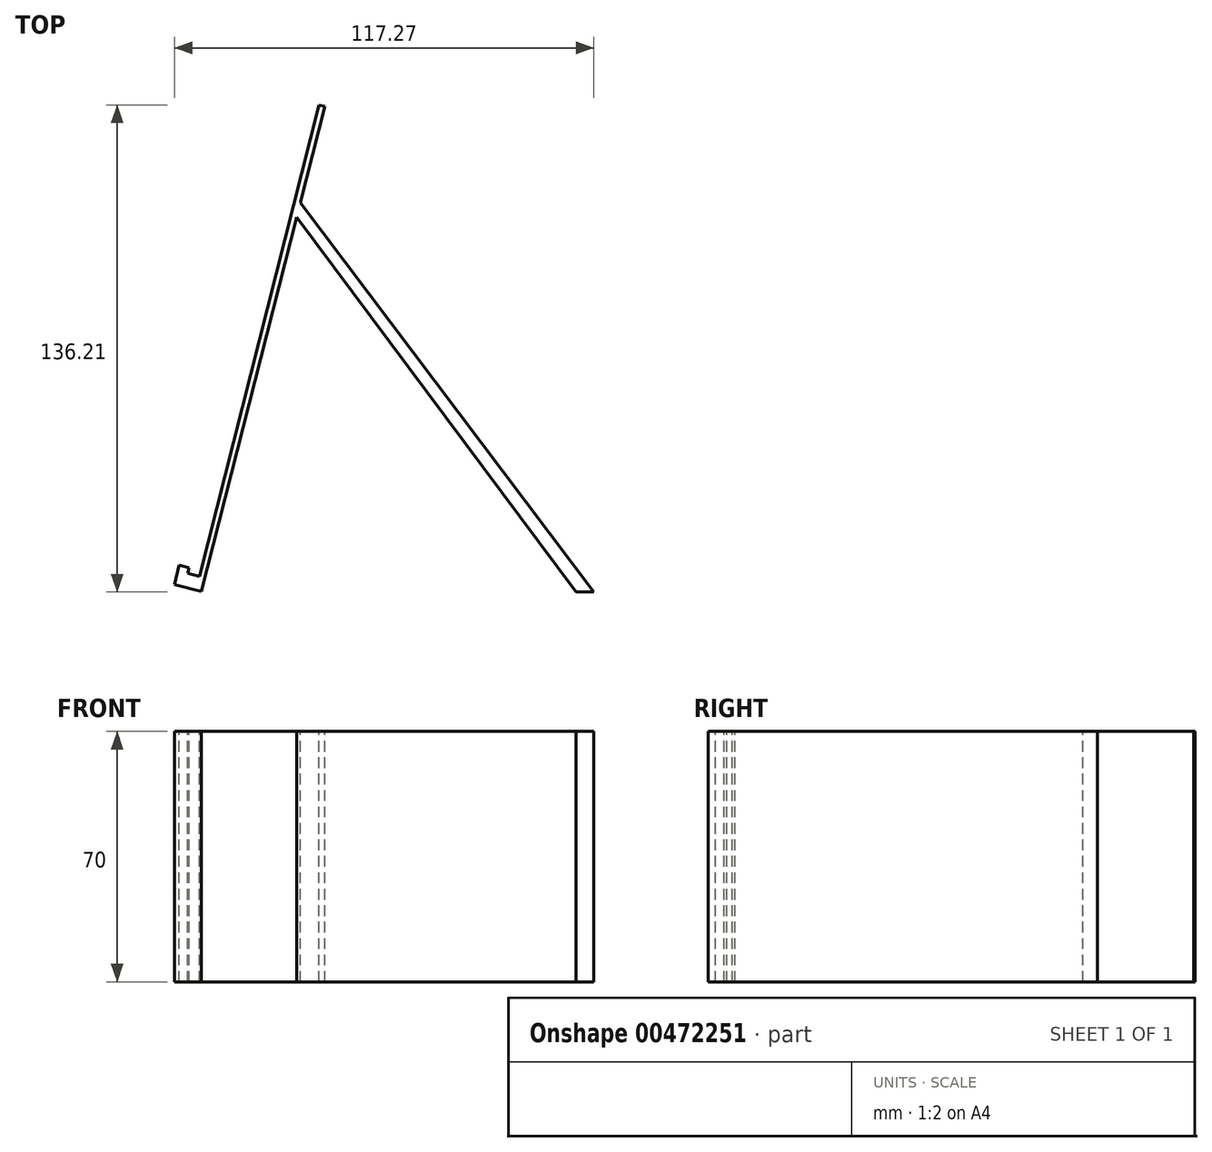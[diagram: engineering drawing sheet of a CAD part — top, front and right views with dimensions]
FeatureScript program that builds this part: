
annotation { "Feature Type Name" : "Feature", "Feature Type Description" : "" }
export const myFeature = defineFeature(function(context is Context, id is Id, definition is map)
    precondition{}
    {
        {
            var Q0;
            Q0=qCreatedBy(makeId("Top.planeOp"),FACE);
            var sketch = newSketch(context, id + "F0", { "sketchPlane" : qUnion([Q0])});
            skLineSegment(sketch, "E0", {"start": v(-45.52, -67.71) * mm, "end": v(-18.92, 37) * mm});
            skLineSegment(sketch, "E1", {"start": v(-18.92, 37) * mm, "end": v(59.18, -67.84) * mm});
            skLineSegment(sketch, "E2", {"start": v(-45.52, -67.71) * mm, "end": v(-53.1, -65.79) * mm});
            skLineSegment(sketch, "E3", {"start": v(-53.1, -65.79) * mm, "end": v(-52.1, -61.9) * mm});
            skLineSegment(sketch, "E4", {"start": v(-49.3, -62.6) * mm, "end": v(-46.09, -63.42) * mm});
            skLineSegment(sketch, "E5", {"start": v(-11.05, 67.98) * mm, "end": v(-12.6, 68.37) * mm});
            skLineSegment(sketch, "E6", {"start": v(-12.6, 68.37) * mm, "end": v(-46.09, -63.42) * mm});
            skPoint(sketch, "E7.endSnap0", {"position": v(-49.3, -66.75) * mm});
            skLineSegment(sketch, "E8", {"start": v(-49.3, -62.6) * mm, "end": v(-48.91, -61.05) * mm});
            skLineSegment(sketch, "E9", {"start": v(-52.1, -61.9) * mm, "end": v(-51.7, -60.35) * mm});
            skLineSegment(sketch, "E10", {"start": v(-48.91, -61.05) * mm, "end": v(-51.7, -60.35) * mm});
            skLineSegment(sketch, "E11", {"start": v(59.18, -67.84) * mm, "end": v(64.18, -67.84) * mm});
            skLineSegment(sketch, "E12", {"start": v(64.18, -67.84) * mm, "end": v(-17.9, 41.02) * mm});
            skLineSegment(sketch, "E13.trimOffspring", {"start": v(-17.9, 41.02) * mm, "end": v(-11.05, 67.98) * mm});
            skSolve(sketch);
        }
        {
            var Q0;
            Q0=makeQuery(id+"F0.imprint","IMPRINT",FACE,{"disambiguationData":[TD([[makeQuery(id+"F0.imprint","IMPRINT",EDGE,{"derivedFrom":sQuery(id+"F0.wireOp",EDGE,"E0")}),1.0]])]});
            extrude(context, id + "F1", {"entities" : qUnion([Q0]), "oppositeDirection" : true, "depth" : 70 * mm});
        }
    });
